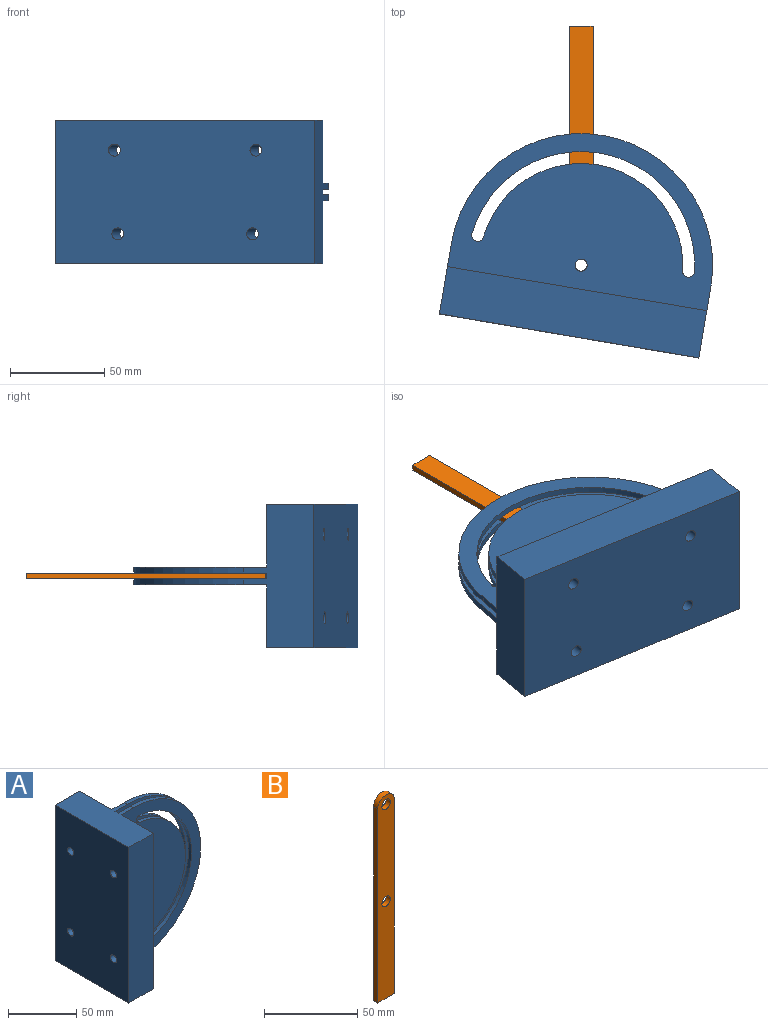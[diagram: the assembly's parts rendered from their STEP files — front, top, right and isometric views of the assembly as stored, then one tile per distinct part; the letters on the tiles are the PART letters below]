
ASSEMBLY  parts=2 mates=1
PART A: 28 faces, bbox 108x76.2x139.7 mm
  f0: cylinder r=3.17mm len=6.33mm, axis (0,1,0), area 31.7mm2, adj f1,f6,f15,f26
  f1: cylinder r=53.98mm len=107.28mm, axis (0,1,0), area 500.2mm2, adj f0,f2,f15,f26
  f2: cylinder r=3.17mm len=6.33mm, axis (0,1,0), area 31.7mm2, adj f1,f6,f15,f26
  f3: plane 76.2x38.1mm, normal (0,0,-1), area 2016.1mm2, adj f4,f11,f14,f15,f16,f17,f21,f23
  f4: cylinder r=69.85mm len=139.7mm, axis (0,1,0), area 696.7mm2, adj f3,f5,f15,f26
  f5: plane 76.2x38.1mm, normal (0,0,1), area 2016.1mm2, adj f4,f11,f14,f15,f16,f17,f21,f23
  f6: cylinder r=60.32mm len=119.9mm, axis (0,1,0), area 559.1mm2, adj f0,f2,f15,f26
  f7: cylinder r=3.17mm len=6.35mm, axis (0,1,0), area 63.3mm2, adj f15,f26
  f8: cylinder r=3.17mm len=6.33mm, axis (0,1,0), area 31.7mm2, adj f9,f12,f14,f27
  f9: cylinder r=53.98mm len=107.28mm, axis (0,1,0), area 500.2mm2, adj f8,f10,f14,f27
  f10: cylinder r=3.17mm len=6.33mm, axis (0,1,0), area 31.7mm2, adj f9,f12,f14,f27
  f11: cylinder r=69.85mm len=139.7mm, axis (0,1,0), area 696.7mm2, adj f3,f5,f14,f27
  f12: cylinder r=60.32mm len=119.9mm, axis (0,1,0), area 559.1mm2, adj f8,f10,f14,f27
  f13: cylinder r=3.17mm len=6.35mm, axis (0,1,0), area 63.3mm2, adj f14,f27
  f14: plane 139.7x82.55mm, normal (0,-1,0), area 8315.5mm2, adj f3,f5,f8,f9,f10,f11,f12,f13
  f15: plane 139.7x82.55mm, normal (0,1,0), area 8315.5mm2, adj f0,f1,f2,f3,f4,f5,f6,f7
  f16: plane 139.7x33.34mm, normal (1,0,0), area 4593.9mm2, adj f3,f5,f15,f17,f18,f22
  f17: plane 139.7x25.4mm, normal (0,1,0), area 3548.4mm2, adj f3,f5,f16,f23
  f18: cylinder r=3.17mm len=25.4mm, axis (1,0,0), area 506.7mm2, adj f16,f23
  f19: cylinder r=3.17mm len=25.4mm, axis (1,0,0), area 506.7mm2, adj f23,f24
  f20: cylinder r=3.17mm len=25.4mm, axis (1,0,0), area 506.7mm2, adj f23,f24
  f21: plane 139.7x25.4mm, normal (0,-1,0), area 3548.4mm2, adj f3,f5,f23,f24
  f22: cylinder r=3.17mm len=25.4mm, axis (1,0,0), area 506.7mm2, adj f16,f23
  f23: plane 139.7x76.2mm, normal (-1,0,0), area 10518.5mm2, adj f3,f5,f17,f18,f19,f20,f21,f22
  f24: plane 139.7x33.34mm, normal (1,0,0), area 4593.9mm2, adj f3,f5,f14,f19,f20,f21
  f25: plane 139.7x3.18mm, normal (1,0,0), area 443.5mm2, adj f3,f5,f26,f27
  f26: plane 139.7x82.55mm, normal (0,-1,0), area 8315.5mm2, adj f0,f1,f2,f3,f4,f5,f6,f7
  f27: plane 139.7x82.55mm, normal (0,1,0), area 8315.5mm2, adj f3,f5,f8,f9,f10,f11,f12,f13
PART B: 8 faces, bbox 12.7x3.2x133.4 mm
  f0: plane 12.7x3.18mm, normal (0,0,-1), area 40.3mm2, adj f1,f4,f6,f7
  f1: plane 127x3.18mm, normal (1,0,0), area 403.2mm2, adj f0,f2,f6,f7
  f2: cylinder r=6.35mm len=12.7mm, axis (0,1,0), area 63.3mm2, adj f1,f4,f6,f7
  f3: cylinder r=3.17mm len=6.35mm, axis (0,1,0), area 63.3mm2, adj f6,f7
  f4: plane 127x3.18mm, normal (-1,0,0), area 403.2mm2, adj f0,f2,f6,f7
  f5: cylinder r=3.17mm len=6.35mm, axis (0,1,0), area 63.3mm2, adj f6,f7
  f6: plane 133.35x12.7mm, normal (0,-1,0), area 1612.9mm2, adj f0,f1,f2,f3,f4,f5
  f7: plane 133.35x12.7mm, normal (0,1,0), area 1612.9mm2, adj f0,f1,f2,f3,f4,f5
PLACE A rot(axis=(-0.64,-0.54,0.54),114.6deg) t=(0,-127,0)mm
PLACE B rot(axis=(0,-0.71,0.71),180deg) t=(0,-63.5,0)mm
MATE revolute B.f5 <-> A.f7  axis (0,0,1) through (0,-127,1.59)mm
